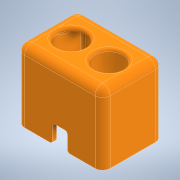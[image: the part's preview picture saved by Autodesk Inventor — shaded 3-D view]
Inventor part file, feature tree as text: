
AUTODESK INVENTOR PART (.ipt)
format: ipt  version: 2021 (Build 250183000, 183)  size: 361,472 bytes
history: native  units: mm
features: extrude x6, sketch x6, fillet x4
ambient origin geometry x8: Origin, YZ Plane, XZ Plane, XY Plane, X Axis, Y Axis, Z Axis, Center Point
bodies: Solid1 (feature_tree)
feature tree (16):
  extrude  "Extrusion1"  Depth=10.3mm
  extrude  "Extrusion2"  Depth=12.0mm
  fillet  "Fillet1"  Radius=14.0mm
  extrude  "Extrusion3"  Depth=5.6mm
  extrude  "Extrusion4"  Depth=1.5mm
  extrude  "Extrusion5"  Depth=1.0mm
  fillet  "Fillet5"  Radius=9.4mm
  fillet  "Fillet6"  Radius=1.0mm
  extrude  "Extrusion6"  Depth=3.0mm
  fillet  "Fillet7"  Radius=0.5mm
  sketch  "Sketch1"  dims[d0=15.2mm d1=10.3mm]
  sketch  "Sketch2"  dims[d2=17.0mm d3=12.0mm d4=14.0mm d5=0.0mm]
  sketch  "Sketch3"  dims[d6=7.0mm d7=0.0mm d8=5.6mm]
  sketch  "Sketch4"  dims[d10=7.5mm d11=1.5mm]
  sketch  "Sketch5"  dims[d13=6.0mm d14=0.0mm d16=1.0mm d17=9.4mm d18=0.0mm d20=1.0mm]
  sketch  "Sketch6"  dims[d21=9.8mm d22=0.0mm d25=3.0mm d26=0.5mm d27=0.3mm d28=9.5mm d29=0.0mm d31=3.0mm d32=0.5mm d33=0.5mm d34=0.872665mm d35=0.5mm d36=0.872665mm]
